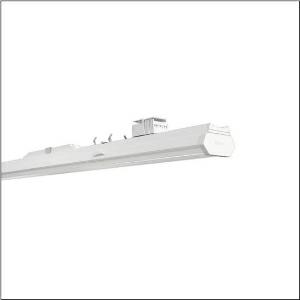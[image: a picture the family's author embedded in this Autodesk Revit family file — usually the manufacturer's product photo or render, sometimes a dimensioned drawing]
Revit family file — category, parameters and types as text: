
# Revit family: licross_11_protected_tw_51tp12tnt85x
name_source: partatom
category: Lighting Fixtures
units: mm (PartAtom-declared; Revit-internal decimal feet)

## family parameters
Cut with Voids When Loaded = No
Host = Face
Light Source = No
Part Type = Normal
Room Calculation Point = No
Round Connector Dimension = Use Diameter
Shared = No

## types (1)
- --- (1 x LED 2700 K ... 6500 K, 8840 lm, 56 W, 2700K)
    Apparent Load = 56 VA
    CIE Flux Codes = 70 91 97 98 100
    Color Rendering = 80
    Color Temperature = 2700K
    Default Elevation = 1800 mm
    Description = Licross 11 Protected TW, luminaire insert, of sheet steel, galvanised, coil coated, white, length: 1.500mm, width: 90mm, height: 101mm, LED rated luminous flux: 8.840lm, light colour: 8tw, SDCM (Standard Deviation of Colour Matching)MacAdam ≤ 2 SDCM (initial), control gear: DALI DT8, with plug, 5-pole, with phase selection, mains connection: 220..240V, AC, 50/60Hz, rated input power: 56W, internal wiring halogen-free, primary optical cover: cover, of PMMA, light emission: direct distribution, primary light characteristic: symmetric, protection rating (complete): IP64, insulation class (complete): insulation class I (protective earthing), certification: CE, ENEC, VDE, UKCA, protection symbol: D if used in an environment with conductive dust loads with corresponding accessories, impact resistance: IK06, permissible ambient temperature for indoor applications: -25..+35°C, corresponds to IFS (International Featured Standards) requirements for safety and quality in the food industry, reducing of maximum allowable ambient temperature of 5°C with ceiling mounting, LABS conformity tested according to VDMA 24364:2018-05, The light source and the operating device comply with the requirements of the Ecodesign Regulation (EU) 2019/2020 and are replaceable in accordance with this regulation, packaging unit: 1 piece
    Height = 92 mm
    Lamp = 1 x LED 2700 K ... 6500 K
    Lamp Light Flux = 8840 lm
    Lamp Power = 56 W
    Lamp count = 1
    Length = 1500 mm
    Luminous efficacy = 158 lm/W
    Manufacturer = Siteco
    ModVariant = No
    Model = 51TP12TNT85X
    Mounting Place = Ceiling
    Mounting Type = Pendant
    Number of Poles = 1
    OnlyDefault = Yes
    Power Factor = 1
    Product Name = Licross 11 Protected TW
    Product group = luminaire insert | ceiling pendant
    ProductGroupID = 901
    Protection Class = Protection class I
    Protection Degree = IP 64
    RLX_Detail_Level = 1
    RLX_Emergency_Light_Flux = 0 lm
    RLX_Emergency_Type = 0
    RLX_Emergency_Type_DB = No
    RlxData = <blob elided: 20981 chars, md5=0ea3fb2e>
    Socket = socket
    Standby Power = 0 W
    System Light Flux = 8840 lm
    System Power = 56 W
    Type Comments = individual setting: CCT=2700K
    Type Image = l_1256148.jpg
    URL = http://relux.com
    VarID = @adj_056159
    Voltage = 0 V
    Weight = 0.00 kg
    Width = 88 mm

## geometry (parser evidence)
native form markers: Blend x4, Sweep x11
no freeform markers — native parametric forms only
